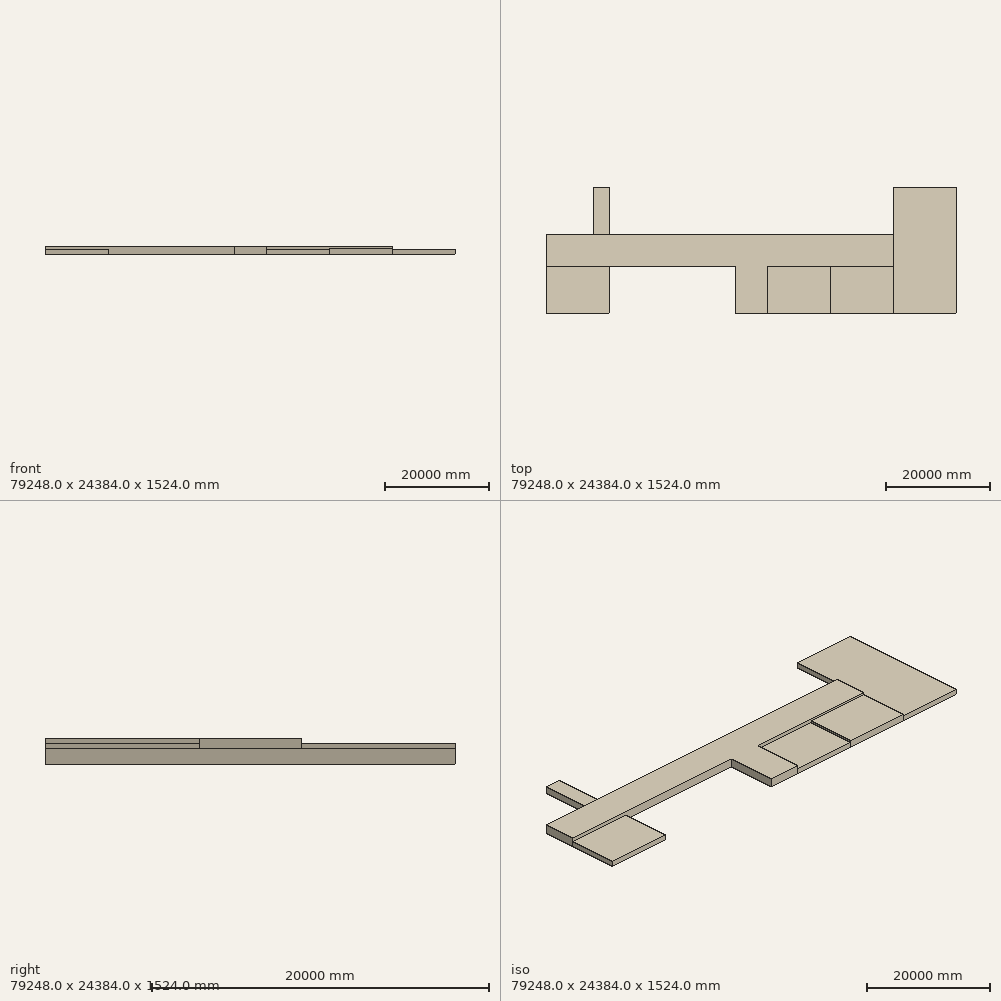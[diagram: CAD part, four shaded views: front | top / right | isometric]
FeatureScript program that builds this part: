
annotation { "Feature Type Name" : "Feature", "Feature Type Description" : "" }
export const myFeature = defineFeature(function(context is Context, id is Id, definition is map)
    precondition{}
    {
        {
            var Q0;
            Q0=qCreatedBy(makeId("Top.planeOp"),FACE);
            var sketch = newSketch(context, id + "F0", { "sketchPlane" : qUnion([Q0])});
            skLineSegment(sketch, "E0.bottom", {"start": v(39624, -12192) * mm, "end": v(-39624, -12192) * mm});
            skLineSegment(sketch, "E0.top", {"start": v(39624, 12192) * mm, "end": v(-39624, 12192) * mm});
            skLineSegment(sketch, "E0.left", {"start": v(39624, -12192) * mm, "end": v(39624, 12192) * mm});
            skLineSegment(sketch, "E0.right", {"start": v(-39624, -12192) * mm, "end": v(-39624, 12192) * mm});
            skPoint(sketch, "E0.middle", {"position": v(0, 0) * mm});
            skLineSegment(sketch, "E1", {"start": v(-39624, -3048) * mm, "end": v(-27432, -3048) * mm});
            skLineSegment(sketch, "E2", {"start": v(-27432, -3048) * mm, "end": v(-27432, -12192) * mm});
            skLineSegment(sketch, "E3.bottom", {"start": v(-39624, 12192) * mm, "end": v(-30480, 12192) * mm});
            skLineSegment(sketch, "E3.top", {"start": v(-39624, 3048) * mm, "end": v(-30480, 3048) * mm});
            skLineSegment(sketch, "E3.left", {"start": v(-39624, 12192) * mm, "end": v(-39624, 3048) * mm});
            skLineSegment(sketch, "E3.right", {"start": v(-30480, 12192) * mm, "end": v(-30480, 3048) * mm});
            skLineSegment(sketch, "E4", {"start": v(-30480, 3048) * mm, "end": v(-27432, 3048) * mm});
            skLineSegment(sketch, "E5", {"start": v(-27432, 3048) * mm, "end": v(-27432, 12192) * mm});
            skLineSegment(sketch, "E6.bottom", {"start": v(-27432, 12192) * mm, "end": v(-15240, 12192) * mm});
            skLineSegment(sketch, "E6.top", {"start": v(-27432, 3048) * mm, "end": v(-15240, 3048) * mm});
            skLineSegment(sketch, "E6.left", {"start": v(-27432, 12192) * mm, "end": v(-27432, 3048) * mm});
            skLineSegment(sketch, "E6.right", {"start": v(-15240, 12192) * mm, "end": v(-15240, 3048) * mm});
            skLineSegment(sketch, "E7.bottom", {"start": v(-27432, -12192) * mm, "end": v(-15240, -12192) * mm});
            skLineSegment(sketch, "E7.top", {"start": v(-27432, -3048) * mm, "end": v(-15240, -3048) * mm});
            skLineSegment(sketch, "E7.left", {"start": v(-27432, -12192) * mm, "end": v(-27432, -3048) * mm});
            skLineSegment(sketch, "E7.right", {"start": v(-15240, -12192) * mm, "end": v(-15240, -3048) * mm});
            skLineSegment(sketch, "E8.bottom", {"start": v(-15240, 12192) * mm, "end": v(-3048, 12192) * mm});
            skLineSegment(sketch, "E8.top", {"start": v(-15240, 3048) * mm, "end": v(-3048, 3048) * mm});
            skLineSegment(sketch, "E8.right", {"start": v(-3048, 12192) * mm, "end": v(-3048, 3048) * mm});
            skLineSegment(sketch, "E9.bottom", {"start": v(-15240, -12192) * mm, "end": v(-3048, -12192) * mm});
            skLineSegment(sketch, "E9.top", {"start": v(-15240, -3048) * mm, "end": v(-3048, -3048) * mm});
            skLineSegment(sketch, "E9.right", {"start": v(-3048, -12192) * mm, "end": v(-3048, -3048) * mm});
            skPoint(sketch, "E10.oppositeSnap0", {"position": v(0, 12192) * mm});
            skLineSegment(sketch, "E10.bottom", {"start": v(-3048, 12192) * mm, "end": v(0, 12192) * mm});
            skLineSegment(sketch, "E10.top", {"start": v(-3048, 3048) * mm, "end": v(0, 3048) * mm});
            skLineSegment(sketch, "E10.right", {"start": v(0, 12192) * mm, "end": v(0, 3048) * mm});
            skLineSegment(sketch, "E11.bottom", {"start": v(0, 12192) * mm, "end": v(3048, 12192) * mm});
            skLineSegment(sketch, "E11.top", {"start": v(0, 3048) * mm, "end": v(3048, 3048) * mm});
            skLineSegment(sketch, "E11.right", {"start": v(3048, 12192) * mm, "end": v(3048, 3048) * mm});
            skLineSegment(sketch, "E12.bottom", {"start": v(3048, 12192) * mm, "end": v(15240, 12192) * mm});
            skLineSegment(sketch, "E12.top", {"start": v(3048, 3048) * mm, "end": v(15240, 3048) * mm});
            skLineSegment(sketch, "E12.right", {"start": v(15240, 12192) * mm, "end": v(15240, 3048) * mm});
            skLineSegment(sketch, "E13.bottom", {"start": v(15240, 12192) * mm, "end": v(27432, 12192) * mm});
            skLineSegment(sketch, "E13.top", {"start": v(15240, 3048) * mm, "end": v(27432, 3048) * mm});
            skLineSegment(sketch, "E13.right", {"start": v(27432, 12192) * mm, "end": v(27432, 3048) * mm});
            skLineSegment(sketch, "E14", {"start": v(27432, 3048) * mm, "end": v(27432, -12192) * mm});
            skLineSegment(sketch, "E15.bottom", {"start": v(3048, -3048) * mm, "end": v(15240, -3048) * mm});
            skLineSegment(sketch, "E15.top", {"start": v(3048, -12192) * mm, "end": v(15240, -12192) * mm});
            skLineSegment(sketch, "E15.left", {"start": v(3048, -3048) * mm, "end": v(3048, -12192) * mm});
            skLineSegment(sketch, "E15.right", {"start": v(15240, -3048) * mm, "end": v(15240, -12192) * mm});
            skLineSegment(sketch, "E16", {"start": v(15240, -3048) * mm, "end": v(27432, -3048) * mm});
            skSolve(sketch);
        }
        {
            var Q0;
            Q0=makeQuery(id+"F0.imprint","IMPRINT",FACE,{"disambiguationData":[TD([[makeQuery(id+"F0.imprint","IMPRINT",EDGE,{"derivedFrom":sQuery(id+"F0.wireOp",EDGE,"E3.bottom")}),-1.0]])]});
            var Q1;
            Q1=makeQuery(id+"F0.imprint","IMPRINT",FACE,{"disambiguationData":[TD([[makeQuery(id+"F0.imprint","IMPRINT",EDGE,{"derivedFrom":sQuery(id+"F0.wireOp",EDGE,"E15.bottom")}),-1.0]])]});
            var Q2;
            Q2=makeQuery(id+"F0.imprint","IMPRINT",FACE,{"disambiguationData":[TD([[makeQuery(id+"F0.imprint","IMPRINT",EDGE,{"derivedFrom":sQuery(id+"F0.wireOp",EDGE,"E6.bottom")}),-1.0]])]});
            var Q3;
            Q3=makeQuery(id+"F0.imprint","IMPRINT",FACE,{"disambiguationData":[TD([[makeQuery(id+"F0.imprint","IMPRINT",EDGE,{"derivedFrom":sQuery(id+"F0.wireOp",EDGE,"E12.bottom")}),-1.0]])]});
            var Q4;
            Q4=makeQuery(id+"F0.imprint","IMPRINT",FACE,{"disambiguationData":[TD([[makeQuery(id+"F0.imprint","IMPRINT",EDGE,{"derivedFrom":sQuery(id+"F0.wireOp",EDGE,"E10.bottom")}),-1.0]])]});
            var Q5;
            {var subQ4=sQuery(id+"F0.wireOp",EDGE,"E1");Q5=makeQuery(id+"F0.imprint","IMPRINT",FACE,{"disambiguationData":[TD([[makeQuery(id+"F0.imprint","IMPRINT",EDGE,{"derivedFrom":subQ4}),-1.0]])]});}
            var Q6;
            Q6=makeQuery(id+"F0.imprint","IMPRINT",FACE,{"disambiguationData":[TD([[makeQuery(id+"F0.imprint","IMPRINT",EDGE,{"derivedFrom":sQuery(id+"F0.wireOp",EDGE,"E9.bottom")}),1.0]])]});
            var Q7;
            {var subQ0=sQuery(id+"F0.wireOp",EDGE,"E0.left");Q7=makeQuery(id+"F0.imprint","IMPRINT",FACE,{"disambiguationData":[TD([[makeQuery(id+"F0.imprint","IMPRINT",EDGE,{"derivedFrom":subQ0}),1.0]])]});}
            extrude(context, id + "F1", {"entities" : qUnion([Q0, Q1, Q2, Q3, Q4, Q5, Q6, Q7]), "depth" : 914.4 * mm, "offsetDistance" : 30.48 * mm});
        }
        {
            var Q0;
            {var subQ3=sQuery(id+"F0.wireOp",EDGE,"E15.right");Q0=makeQuery(id+"F0.imprint","IMPRINT",FACE,{"disambiguationData":[TD([[makeQuery(id+"F0.imprint","IMPRINT",EDGE,{"derivedFrom":subQ3}),1.0]])]});}
            var Q1;
            Q1=makeQuery(id+"F0.imprint","IMPRINT",FACE,{"disambiguationData":[TD([[makeQuery(id+"F0.imprint","IMPRINT",EDGE,{"derivedFrom":sQuery(id+"F0.wireOp",EDGE,"E13.bottom")}),-1.0]])]});
            var Q2;
            Q2=makeQuery(id+"F0.imprint","IMPRINT",FACE,{"disambiguationData":[TD([[makeQuery(id+"F0.imprint","IMPRINT",EDGE,{"derivedFrom":sQuery(id+"F0.wireOp",EDGE,"E8.bottom")}),-1.0]])]});
            var Q3;
            Q3=makeQuery(id+"F0.imprint","IMPRINT",FACE,{"disambiguationData":[TD([[makeQuery(id+"F0.imprint","IMPRINT",EDGE,{"derivedFrom":sQuery(id+"F0.wireOp",EDGE,"E11.bottom")}),-1.0]])]});
            var Q4;
            {var subQ0=sQuery(id+"F0.wireOp",EDGE,"E3.right");Q4=makeQuery(id+"F0.imprint","IMPRINT",FACE,{"disambiguationData":[TD([[makeQuery(id+"F0.imprint","IMPRINT",EDGE,{"derivedFrom":subQ0}),1.0]])]});}
            var Q5;
            Q5=makeQuery(id+"F0.imprint","IMPRINT",FACE,{"disambiguationData":[TD([[makeQuery(id+"F0.imprint","IMPRINT",EDGE,{"derivedFrom":sQuery(id+"F0.wireOp",EDGE,"E7.bottom")}),1.0]])]});
            extrude(context, id + "F2", {"entities" : qUnion([Q0, Q1, Q2, Q3, Q4, Q5]), "depth" : 1219.2 * mm, "offsetDistance" : 30.48 * mm});
        }
        {
            var Q0;
            {var subQ5=sQuery(id+"F0.wireOp",EDGE,"E1");Q0=makeQuery(id+"F0.imprint","IMPRINT",FACE,{"disambiguationData":[TD([[makeQuery(id+"F0.imprint","IMPRINT",EDGE,{"derivedFrom":subQ5}),1.0]])]});}
            extrude(context, id + "F3", {"entities" : qUnion([Q0]), "depth" : 1524 * mm, "offsetDistance" : 30.48 * mm});
        }
    });
